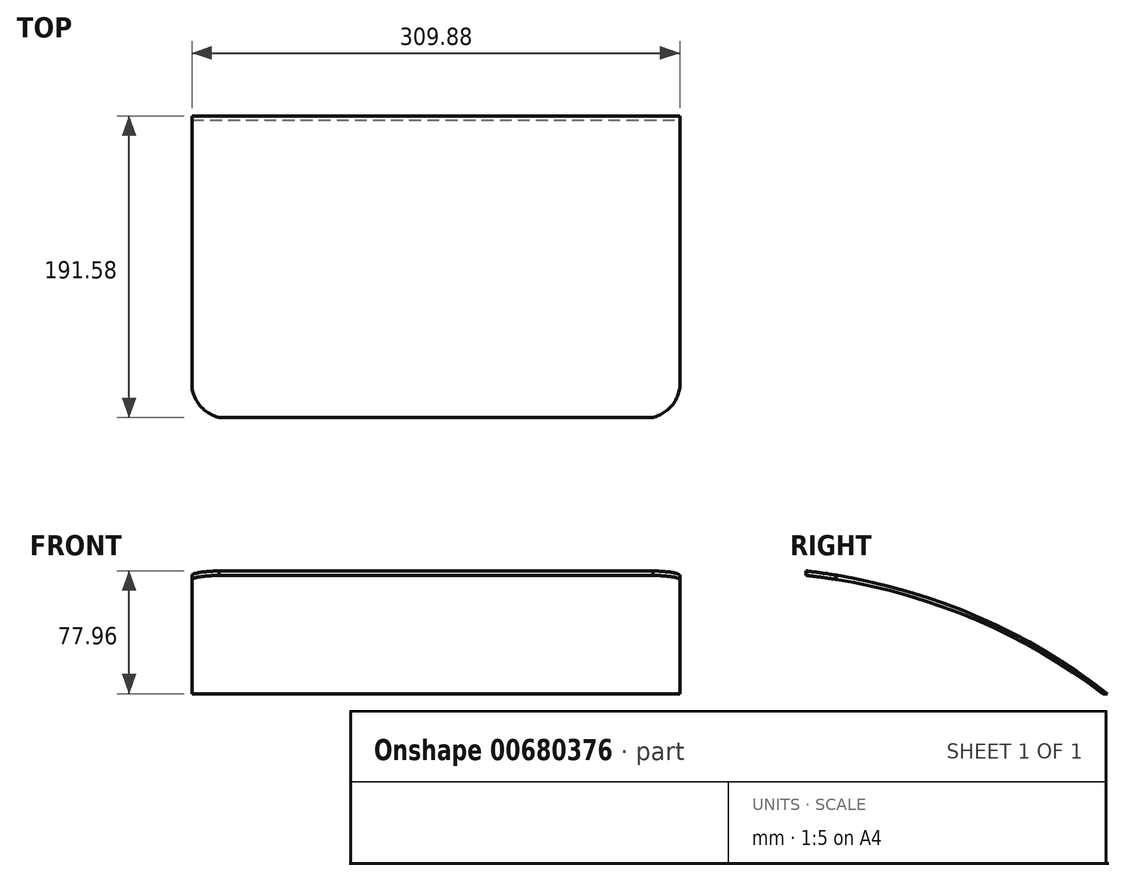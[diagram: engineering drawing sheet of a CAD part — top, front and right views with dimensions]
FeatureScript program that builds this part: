
annotation { "Feature Type Name" : "Feature", "Feature Type Description" : "" }
export const myFeature = defineFeature(function(context is Context, id is Id, definition is map)
    precondition{}
    {
        {
            var Q0;
            Q0=qCreatedBy(makeId("Right.planeOp"),FACE);
            var sketch = newSketch(context, id + "F0", { "sketchPlane" : qUnion([Q0])});
            skArc(sketch, "E0", {"start": v(0, 0) * mm, "mid": v(-89.3, 50.4) * mm, "end": v(-188.79, 75.16) * mm});
            skLineSegment(sketch, "E1", {"start": v(-188.79, 75.16) * mm, "end": v(-188.79, 77.96) * mm});
            skLineSegment(sketch, "E2", {"start": v(0, 0) * mm, "end": v(2.8, 0) * mm});
            skArc(sketch, "E3", {"start": v(2.8, 0) * mm, "mid": v(-87.6, 52.23) * mm, "end": v(-188.79, 77.96) * mm});
            skSolve(sketch);
        }
        {
            var Q0;
            Q0=qSketchRegion(id+"F0",true);
            extrude(context, id + "F1", {"entities" : qUnion([Q0]), "oppositeDirection" : true, "depth" : 154.94 * mm, "offsetDistance" : 25.4 * mm, "hasSecondDirection" : true, "secondDirectionOppositeDirection" : false, "secondDirectionDepth" : 154.94 * mm});
        }
        {
            var Q0;
            Q0=qCreatedBy(makeId("Top.planeOp"),FACE);
            var sketch = newSketch(context, id + "F2", { "sketchPlane" : qUnion([Q0])});
            skArc(sketch, "E4", {"start": v(-154.94, -163.21) * mm, "mid": v(-147.62, -183.51) * mm, "end": v(-126.7, -188.79) * mm});
            skLineSegment(sketch, "E5", {"start": v(-154.94, -163.21) * mm, "end": v(-161.34, -163.21) * mm});
            skLineSegment(sketch, "E6", {"start": v(-161.34, -163.21) * mm, "end": v(-161.34, -196.93) * mm});
            skLineSegment(sketch, "E7", {"start": v(-161.34, -196.93) * mm, "end": v(-120.77, -196.93) * mm});
            skLineSegment(sketch, "E8", {"start": v(-120.77, -196.93) * mm, "end": v(-126.7, -188.79) * mm});
            skLineSegment(sketch, "E9.MirrorCS", {"start": v(120.77, -196.93) * mm, "end": v(126.7, -188.79) * mm});
            skLineSegment(sketch, "E10.MirrorCS", {"start": v(161.34, -163.21) * mm, "end": v(161.34, -196.93) * mm});
            skArc(sketch, "E11.MirrorCS", {"start": v(154.94, -163.21) * mm, "mid": v(147.62, -183.51) * mm, "end": v(126.7, -188.79) * mm});
            skLineSegment(sketch, "E12.MirrorCS", {"start": v(161.34, -196.93) * mm, "end": v(120.77, -196.93) * mm});
            skLineSegment(sketch, "E13.MirrorCS", {"start": v(154.94, -163.21) * mm, "end": v(161.34, -163.21) * mm});
            skSolve(sketch);
        }
        {
            var Q0;
            Q0=qSketchRegion(id+"F2",true);
            extrude(context, id + "F3", {"entities" : qUnion([Q0]), "operationType" : NewBodyOperationType.REMOVE, "depth" : 186.18 * mm, "offsetDistance" : 25.4 * mm});
        }
    });
